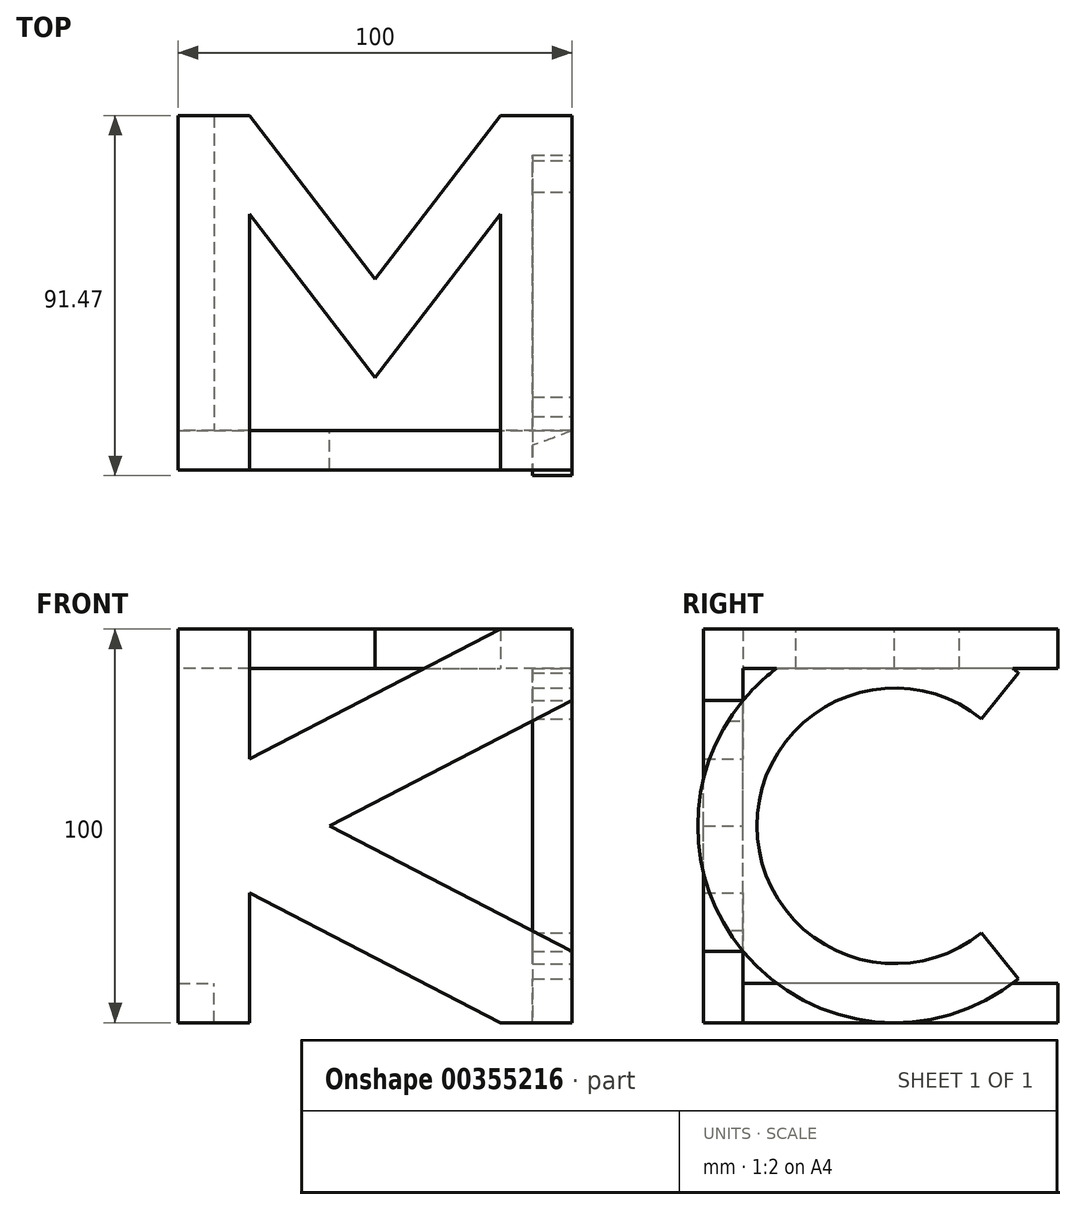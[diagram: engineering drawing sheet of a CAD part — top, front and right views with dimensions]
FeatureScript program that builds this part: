
annotation { "Feature Type Name" : "Feature", "Feature Type Description" : "" }
export const myFeature = defineFeature(function(context is Context, id is Id, definition is map)
    precondition{}
    {
        {
            var Q0;
            Q0=qCreatedBy(makeId("Front.planeOp"),FACE);
            var sketch = newSketch(context, id + "F0", { "sketchPlane" : qUnion([Q0])});
            skLineSegment(sketch, "E0.left", {"start": v(0, 0) * mm, "end": v(0, 100) * mm});
            skLineSegment(sketch, "E1", {"start": v(0, 0) * mm, "end": v(18.13, 0) * mm});
            skLineSegment(sketch, "E2", {"start": v(18.13, 0) * mm, "end": v(18.13, 33) * mm});
            skLineSegment(sketch, "E3", {"start": v(18.13, 33) * mm, "end": v(81.87, 0) * mm});
            skLineSegment(sketch, "E4", {"start": v(81.87, 0) * mm, "end": v(100, 0) * mm});
            skLineSegment(sketch, "E5", {"start": v(100, 18.13) * mm, "end": v(38.46, 50) * mm});
            skLineSegment(sketch, "E6", {"start": v(38.46, 50) * mm, "end": v(100, 81.87) * mm});
            skLineSegment(sketch, "E7", {"start": v(100, 81.87) * mm, "end": v(100, 100) * mm});
            skLineSegment(sketch, "E8", {"start": v(81.87, 100) * mm, "end": v(18.13, 67) * mm});
            skLineSegment(sketch, "E9", {"start": v(18.13, 67) * mm, "end": v(18.13, 100) * mm});
            skLineSegment(sketch, "E10", {"start": v(18.13, 100) * mm, "end": v(0, 100) * mm});
            skLineSegment(sketch, "E11", {"start": v(100, 18.13) * mm, "end": v(100, 0) * mm});
            skLineSegment(sketch, "E12", {"start": v(81.87, 100) * mm, "end": v(100, 100) * mm});
            skSolve(sketch);
        }
        {
            var Q0;
            Q0 = qSketchRegion(id + "F0", true);
            extrude(context, id + "F1", {"entities" : qUnion([Q0]), "depth" : 10 * mm});
        }
        {
            var Q0;
            Q0=makeQuery(id+"F1.opExtrude","SWEPT_FACE",FACE,{"disambiguationData":[OSD([sQuery(id+"F0.wireOp",EDGE,"E7")])]});
            var sketch = newSketch(context, id + "F2", { "sketchPlane" : qUnion([Q0])});
            skArc(sketch, "E13", {"start": v(70, 88.85) * mm, "mid": v(-8.6, 66.7) * mm, "end": v(38.53, 0) * mm});
            skLineSegment(sketch, "E14", {"start": v(0, 100) * mm, "end": v(38.53, 100) * mm});
            skLineSegment(sketch, "E15", {"start": v(38.53, 0) * mm, "end": v(0, 0) * mm});
            skArc(sketch, "E16", {"start": v(38.53, 0) * mm, "mid": v(55.22, 2.87) * mm, "end": v(70, 11.15) * mm});
            skArc(sketch, "E17", {"start": v(60.56, 77.2) * mm, "mid": v(3.53, 50) * mm, "end": v(60.56, 22.8) * mm});
            skLineSegment(sketch, "E18", {"start": v(60.56, 77.2) * mm, "end": v(70, 88.85) * mm});
            skLineSegment(sketch, "E19", {"start": v(60.56, 22.8) * mm, "end": v(70, 11.15) * mm});
            skLineSegment(sketch, "E20", {"start": v(70, 88.85) * mm, "end": v(86.75, 75.29) * mm});
            skLineSegment(sketch, "E21", {"start": v(70, 11.15) * mm, "end": v(85.95, 24.06) * mm});
            skSolve(sketch);
        }
        {
            var Q0;
            Q0 = qSketchRegion(id + "F2", true);
            extrude(context, id + "F3", {"entities" : qUnion([Q0]), "operationType" : NewBodyOperationType.ADD, "oppositeDirection" : true, "depth" : 10 * mm});
        }
        {
            var Q0;
            Q0=makeQuery(id+"F1.opExtrude","SWEPT_FACE",FACE,{"disambiguationData":[OSD([sQuery(id+"F0.wireOp",EDGE,"E10")])]});
            var sketch = newSketch(context, id + "F4", { "sketchPlane" : qUnion([Q0])});
            skLineSegment(sketch, "E22", {"start": v(18.13, -10) * mm, "end": v(18.13, 55) * mm});
            skPoint(sketch, "E22.endSnap0", {"position": v(18.13, -5) * mm});
            skLineSegment(sketch, "E23", {"start": v(18.13, 55) * mm, "end": v(50, 13.47) * mm});
            skLineSegment(sketch, "E24", {"start": v(50, 13.47) * mm, "end": v(81.87, 55) * mm});
            skLineSegment(sketch, "E25", {"start": v(81.87, 55) * mm, "end": v(81.87, -10) * mm});
            skLineSegment(sketch, "E26", {"start": v(81.87, -10) * mm, "end": v(100, -10) * mm});
            skLineSegment(sketch, "E27", {"start": v(100, -10) * mm, "end": v(100, 80) * mm});
            skLineSegment(sketch, "E28", {"start": v(100, 80) * mm, "end": v(81.87, 80) * mm});
            skLineSegment(sketch, "E29", {"start": v(18.13, 80) * mm, "end": v(0, 80) * mm});
            skLineSegment(sketch, "E30", {"start": v(0, 80) * mm, "end": v(0, -10) * mm});
            skLineSegment(sketch, "E31", {"start": v(0, -10) * mm, "end": v(18.13, -10) * mm});
            skLineSegment(sketch, "E32", {"start": v(18.13, 80) * mm, "end": v(50, 38.47) * mm});
            skLineSegment(sketch, "E33", {"start": v(50, 38.47) * mm, "end": v(81.87, 80) * mm});
            skSolve(sketch);
        }
        {
            var Q0;
            Q0 = qSketchRegion(id + "F4", true);
            extrude(context, id + "F5", {"entities" : qUnion([Q0]), "operationType" : NewBodyOperationType.ADD, "oppositeDirection" : true, "depth" : 10 * mm});
        }
        {
            var Q0;
            Q0=makeQuery(id+"F1.opExtrude","CAP_FACE",FACE,{"disambiguationData":[OSD([sQuery(id+"F0.wireOp",EDGE,"E0.left"),sQuery(id+"F0.wireOp",EDGE,"E1"),sQuery(id+"F0.wireOp",EDGE,"E2"),sQuery(id+"F0.wireOp",EDGE,"E3"),sQuery(id+"F0.wireOp",EDGE,"E4"),sQuery(id+"F0.wireOp",EDGE,"E5"),sQuery(id+"F0.wireOp",EDGE,"E6"),sQuery(id+"F0.wireOp",EDGE,"E7"),sQuery(id+"F0.wireOp",EDGE,"E8"),sQuery(id+"F0.wireOp",EDGE,"E9"),sQuery(id+"F0.wireOp",EDGE,"E10"),sQuery(id+"F0.wireOp",EDGE,"E11"),sQuery(id+"F0.wireOp",EDGE,"E12")])],"isStart":true});
            var sketch = newSketch(context, id + "F6", { "sketchPlane" : qUnion([Q0])});
            skPoint(sketch, "E34.oppositeSnap0", {"position": v(-9.07, 0) * mm});
            skLineSegment(sketch, "E34.bottom", {"start": v(0, 0) * mm, "end": v(-9.07, 0) * mm});
            skLineSegment(sketch, "E34.top", {"start": v(0, 10) * mm, "end": v(-9.07, 10) * mm});
            skLineSegment(sketch, "E34.left", {"start": v(0, 0) * mm, "end": v(0, 10) * mm});
            skLineSegment(sketch, "E34.right", {"start": v(-9.07, 0) * mm, "end": v(-9.07, 10) * mm});
            skSolve(sketch);
        }
        {
            var Q0;
            Q0 = qSketchRegion(id + "F6", true);
            extrude(context, id + "F7", {"entities" : qUnion([Q0]), "operationType" : NewBodyOperationType.ADD, "depth" : 80 * mm});
        }
    });
